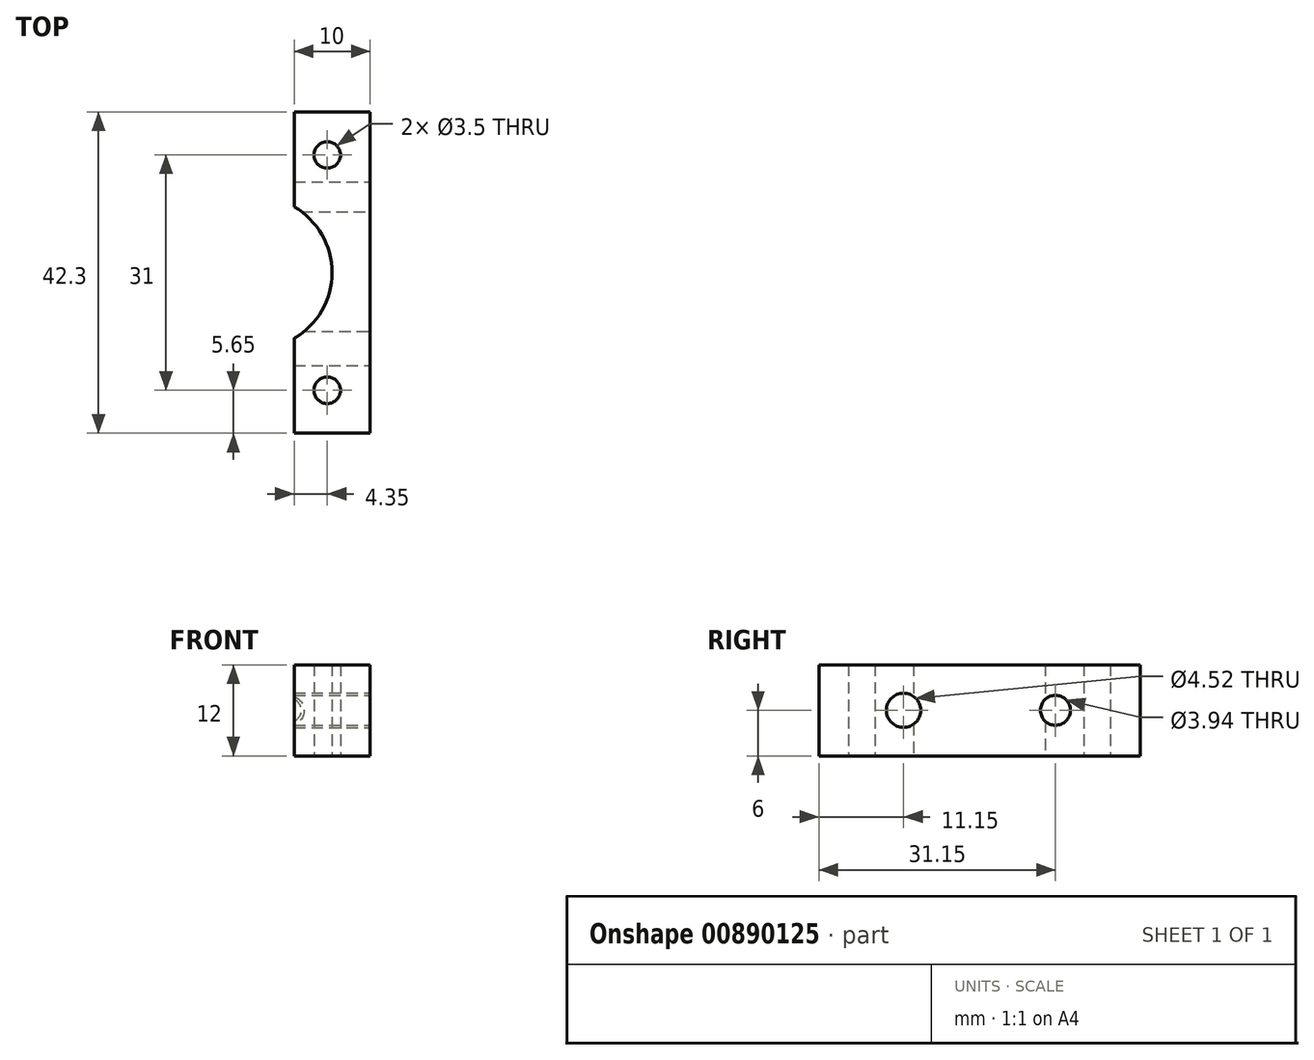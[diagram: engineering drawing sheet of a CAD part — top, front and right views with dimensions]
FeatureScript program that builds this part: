
annotation { "Feature Type Name" : "Feature", "Feature Type Description" : "" }
export const myFeature = defineFeature(function(context is Context, id is Id, definition is map)
    precondition{}
    {
        {
            var Q0;
            Q0=qCreatedBy(makeId("Top.planeOp"),FACE);
            var sketch = newSketch(context, id + "F0", { "sketchPlane" : qUnion([Q0])});
            skCircle(sketch, "E0", {"center": v(-15, 21.15) * mm, "radius": 10 * mm});
            skLineSegment(sketch, "E1", {"start": v(0, 0) * mm, "end": v(-10, 0) * mm});
            skLineSegment(sketch, "E2", {"start": v(-10, 0) * mm, "end": v(-10, 42.3) * mm});
            skLineSegment(sketch, "E3", {"start": v(-10, 42.3) * mm, "end": v(0, 42.3) * mm});
            skLineSegment(sketch, "E4", {"start": v(0, 42.3) * mm, "end": v(0, 0) * mm});
            skCircle(sketch, "E5", {"center": v(-5.65, 36.65) * mm, "radius": 1.75 * mm});
            skCircle(sketch, "E6", {"center": v(-5.65, 5.65) * mm, "radius": 1.75 * mm});
            skSolve(sketch);
        }
        {
            var Q0;
            {var subQ4=sQuery(id+"F0.wireOp",EDGE,"E1");Q0=makeQuery(id+"F0.imprint","IMPRINT",FACE,{"disambiguationData":[TD([[makeQuery(id+"F0.imprint","IMPRINT",EDGE,{"derivedFrom":subQ4}),-1.0]])]});}
            extrude(context, id + "F1", {"entities" : qUnion([Q0]), "depth" : 12 * mm, "offsetDistance" : 25 * mm});
        }
        {
            var Q0;
            Q0=makeQuery(id+"F1.opExtrude","SWEPT_FACE",FACE,{"disambiguationData":[OSD([sQuery(id+"F0.wireOp",EDGE,"E4")])]});
            var sketch = newSketch(context, id + "F2", { "sketchPlane" : qUnion([Q0])});
            skCircle(sketch, "E7", {"center": v(31.15, 6) * mm, "radius": 1.97 * mm});
            skPoint(sketch, "E7.centerSnap0", {"position": v(42.3, 6) * mm});
            skCircle(sketch, "E8", {"center": v(11.15, 6) * mm, "radius": 2.26 * mm});
            skSolve(sketch);
        }
        {
            var Q0;
            Q0 = qSketchRegion(id + "F2", true);
            extrude(context, id + "F3", {"entities" : qUnion([Q0]), "operationType" : NewBodyOperationType.REMOVE, "oppositeDirection" : true, "depth" : 25 * mm, "offsetDistance" : 25 * mm});
        }
    });
